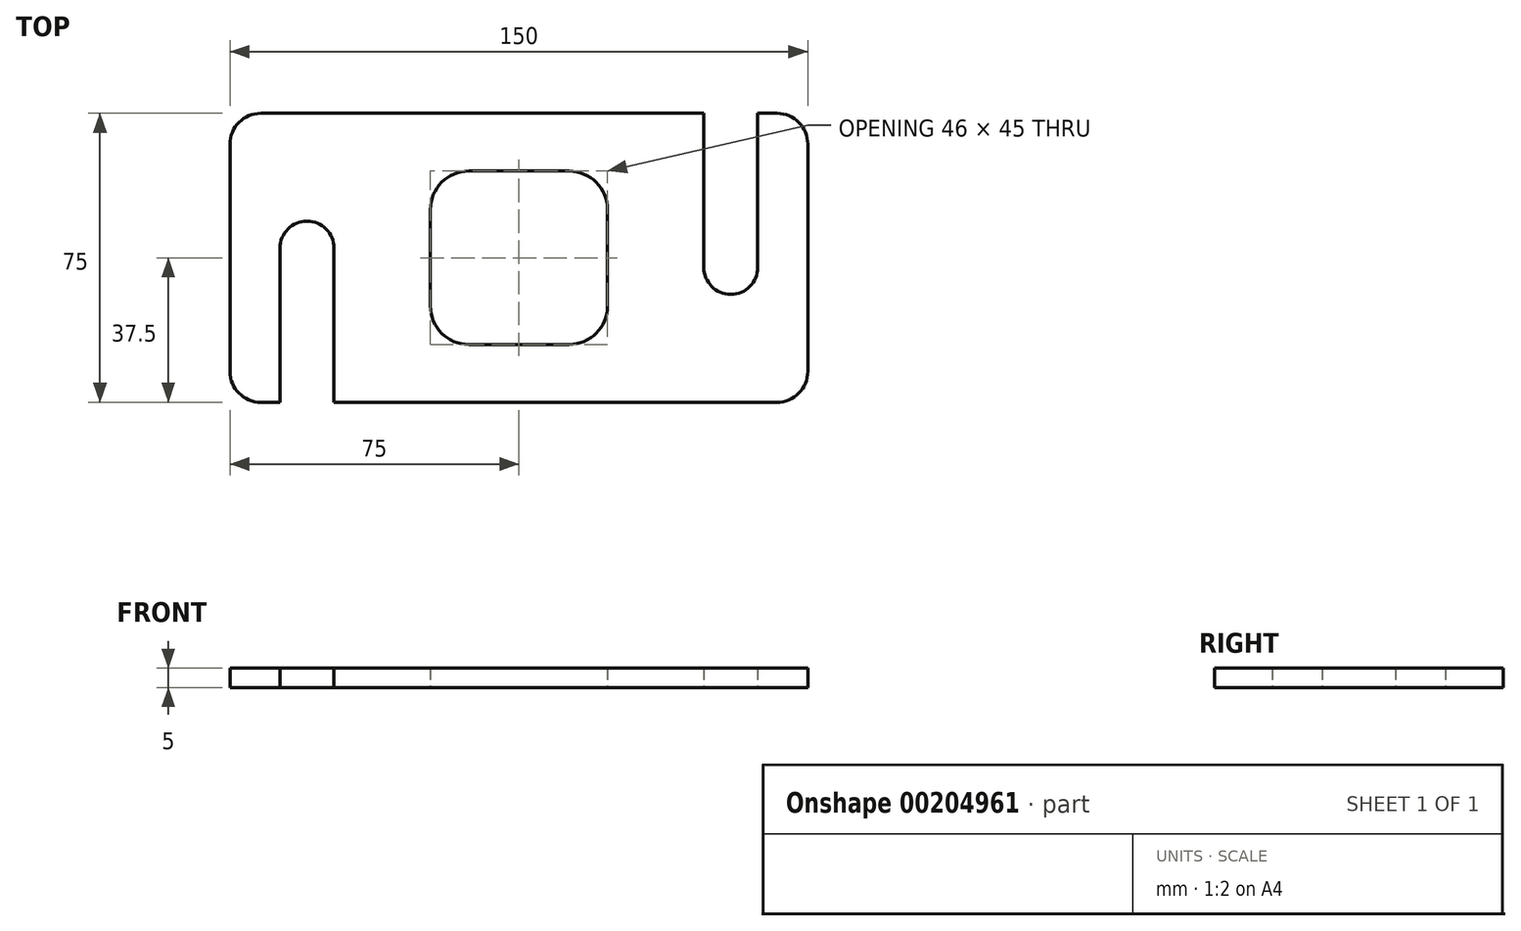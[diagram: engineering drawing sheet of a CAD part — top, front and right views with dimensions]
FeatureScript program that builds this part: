
annotation { "Feature Type Name" : "Feature", "Feature Type Description" : "" }
export const myFeature = defineFeature(function(context is Context, id is Id, definition is map)
    precondition{}
    {
        {
            var Q0;
            Q0=qCreatedBy(makeId("Top.planeOp"),FACE);
            var sketch = newSketch(context, id + "F0", { "sketchPlane" : qUnion([Q0])});
            skLineSegment(sketch, "E0.bottom", {"start": v(0, 0) * mm, "end": v(150, 0) * mm});
            skLineSegment(sketch, "E0.top", {"start": v(0, 75) * mm, "end": v(150, 75) * mm});
            skLineSegment(sketch, "E0.left", {"start": v(0, 0) * mm, "end": v(0, 75) * mm});
            skLineSegment(sketch, "E0.right", {"start": v(150, 0) * mm, "end": v(150, 75) * mm});
            skSolve(sketch);
        }
        {
            var Q0;
            Q0 = qSketchRegion(id + "F0", true);
            extrude(context, id + "F1", {"entities" : qUnion([Q0]), "depth" : 5 * mm});
        }
        {
            var Q0;
            Q0=qCreatedBy(makeId("Top.planeOp"),FACE);
            var sketch = newSketch(context, id + "F2", { "sketchPlane" : qUnion([Q0])});
            skLineSegment(sketch, "E1", {"start": v(13, 0) * mm, "end": v(13, 40) * mm});
            skLineSegment(sketch, "E2", {"start": v(27, 0) * mm, "end": v(27, 40) * mm});
            skArc(sketch, "E3", {"start": v(27, 40) * mm, "mid": v(20, 47) * mm, "end": v(13, 40) * mm});
            skLineSegment(sketch, "E4", {"start": v(13, 0) * mm, "end": v(27, 0) * mm});
            skSolve(sketch);
        }
        {
            var Q0;
            Q0 = qSketchRegion(id + "F2", true);
            extrude(context, id + "F3", {"entities" : qUnion([Q0]), "operationType" : NewBodyOperationType.REMOVE, "endBound" : BoundingType.THROUGH_ALL, "depth" : 25 * mm});
        }
        {
            var Q0;
            Q0=makeQuery(id+"F1.opExtrude","CAP_FACE",FACE,{"disambiguationData":[OSD([sQuery(id+"F0.wireOp",EDGE,"E0.bottom"),sQuery(id+"F0.wireOp",EDGE,"E0.top"),sQuery(id+"F0.wireOp",EDGE,"E0.left"),sQuery(id+"F0.wireOp",EDGE,"E0.right")])],"isStart":true});
            var sketch = newSketch(context, id + "F4", { "sketchPlane" : qUnion([Q0])});
            skLineSegment(sketch, "E5", {"start": v(137, -75) * mm, "end": v(137, -35) * mm});
            skLineSegment(sketch, "E6", {"start": v(123, -75) * mm, "end": v(123, -35) * mm});
            skLineSegment(sketch, "E7", {"start": v(123, -75) * mm, "end": v(137, -75) * mm});
            skArc(sketch, "E8", {"start": v(137, -35) * mm, "mid": v(130, -28) * mm, "end": v(123, -35) * mm});
            skSolve(sketch);
        }
        {
            var Q0;
            Q0 = qSketchRegion(id + "F4", true);
            extrude(context, id + "F5", {"entities" : qUnion([Q0]), "operationType" : NewBodyOperationType.REMOVE, "endBound" : BoundingType.THROUGH_ALL, "oppositeDirection" : true, "depth" : 25 * mm});
        }
        {
            var Q0;
            Q0=makeQuery(id+"F1.opExtrude","CAP_FACE",FACE,{"disambiguationData":[OSD([sQuery(id+"F0.wireOp",EDGE,"E0.bottom"),sQuery(id+"F0.wireOp",EDGE,"E0.top"),sQuery(id+"F0.wireOp",EDGE,"E0.left"),sQuery(id+"F0.wireOp",EDGE,"E0.right")])],"isStart":true});
            var sketch = newSketch(context, id + "F6", { "sketchPlane" : qUnion([Q0])});
            skLineSegment(sketch, "E9.bottom", {"start": v(52, -15) * mm, "end": v(98, -15) * mm});
            skLineSegment(sketch, "E9.top", {"start": v(52, -60) * mm, "end": v(98, -60) * mm});
            skLineSegment(sketch, "E9.left", {"start": v(52, -15) * mm, "end": v(52, -60) * mm});
            skLineSegment(sketch, "E9.right", {"start": v(98, -15) * mm, "end": v(98, -60) * mm});
            skSolve(sketch);
        }
        {
            var Q0;
            Q0 = qSketchRegion(id + "F6", true);
            extrude(context, id + "F7", {"entities" : qUnion([Q0]), "operationType" : NewBodyOperationType.REMOVE, "endBound" : BoundingType.THROUGH_ALL, "oppositeDirection" : true, "depth" : 25 * mm});
        }
        {
            var Q0;
            Q0=makeQuery(id+"F7.boolean.opBoolean","COPY",EDGE,{"derivedFrom":makeQuery(id+"F7.opExtrude","SWEPT_EDGE",EDGE,{"disambiguationData":[OSD([sQuery(id+"F6.wireOp",EDGE,"E9.bottom"),sQuery(id+"F6.wireOp",EDGE,"E9.left")])]})});
            var Q1;
            Q1=makeQuery(id+"F7.boolean.opBoolean","COPY",EDGE,{"derivedFrom":makeQuery(id+"F7.opExtrude","SWEPT_EDGE",EDGE,{"disambiguationData":[OSD([sQuery(id+"F6.wireOp",EDGE,"E9.bottom"),sQuery(id+"F6.wireOp",EDGE,"E9.right")])]})});
            fillet(context, id + "F8", {"entities" : qUnion([Q0, Q1]), "radius" : 10 * mm, "tangentPropagation" : true, "allowEdgeOverflow" : false});
        }
        {
            var Q0;
            Q0=makeQuery(id+"F7.boolean.opBoolean","COPY",EDGE,{"derivedFrom":makeQuery(id+"F7.opExtrude","SWEPT_EDGE",EDGE,{"disambiguationData":[OSD([sQuery(id+"F6.wireOp",EDGE,"E9.top"),sQuery(id+"F6.wireOp",EDGE,"E9.left")])]})});
            var Q1;
            Q1=makeQuery(id+"F7.boolean.opBoolean","COPY",EDGE,{"derivedFrom":makeQuery(id+"F7.opExtrude","SWEPT_EDGE",EDGE,{"disambiguationData":[OSD([sQuery(id+"F6.wireOp",EDGE,"E9.top"),sQuery(id+"F6.wireOp",EDGE,"E9.right")])]})});
            fillet(context, id + "F9", {"entities" : qUnion([Q0, Q1]), "radius" : 10 * mm, "tangentPropagation" : true, "allowEdgeOverflow" : false});
        }
        {
            var Q0;
            Q0=makeQuery(id+"F1.opExtrude","SWEPT_EDGE",EDGE,{"disambiguationData":[OSD([sQuery(id+"F0.wireOp",EDGE,"E0.bottom"),sQuery(id+"F0.wireOp",EDGE,"E0.right")])]});
            fillet(context, id + "F10", {"entities" : qUnion([Q0]), "radius" : 8 * mm, "tangentPropagation" : true, "allowEdgeOverflow" : false});
        }
        {
            var Q0;
            Q0=makeQuery(id+"F1.opExtrude","SWEPT_EDGE",EDGE,{"disambiguationData":[OSD([sQuery(id+"F0.wireOp",EDGE,"E0.top"),sQuery(id+"F0.wireOp",EDGE,"E0.left")])]});
            fillet(context, id + "F11", {"entities" : qUnion([Q0]), "radius" : 8 * mm, "tangentPropagation" : true, "allowEdgeOverflow" : false});
        }
        {
            var Q0;
            Q0=makeQuery(id+"F1.opExtrude","SWEPT_EDGE",EDGE,{"disambiguationData":[OSD([sQuery(id+"F0.wireOp",EDGE,"E0.bottom"),sQuery(id+"F0.wireOp",EDGE,"E0.left")])]});
            fillet(context, id + "F12", {"entities" : qUnion([Q0]), "radius" : 8 * mm, "tangentPropagation" : true, "allowEdgeOverflow" : false});
        }
        {
            var Q0;
            Q0=makeQuery(id+"F1.opExtrude","SWEPT_EDGE",EDGE,{"disambiguationData":[OSD([sQuery(id+"F0.wireOp",EDGE,"E0.top"),sQuery(id+"F0.wireOp",EDGE,"E0.right")])]});
            fillet(context, id + "F13", {"entities" : qUnion([Q0]), "radius" : 8 * mm, "tangentPropagation" : true, "allowEdgeOverflow" : false});
        }
    });
